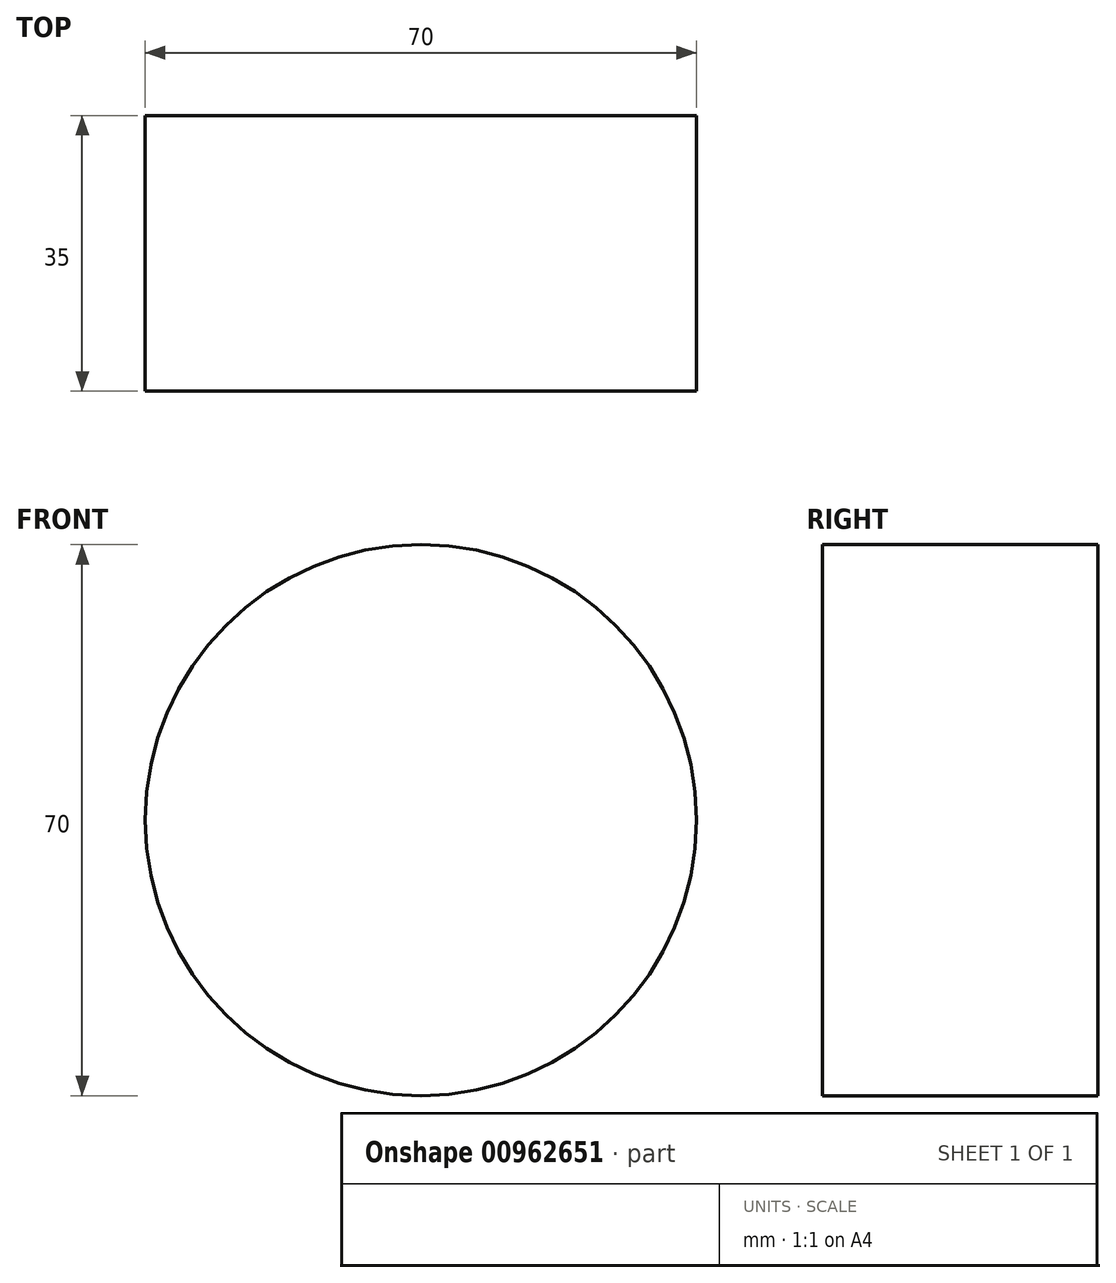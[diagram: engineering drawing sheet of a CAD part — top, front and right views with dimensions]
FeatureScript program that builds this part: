
annotation { "Feature Type Name" : "Feature", "Feature Type Description" : "" }
export const myFeature = defineFeature(function(context is Context, id is Id, definition is map)
    precondition{}
    {
        {
            var Q0;
            Q0=qCreatedBy(makeId("Front.planeOp"),FACE);
            var sketch = newSketch(context, id + "F0", { "sketchPlane" : qUnion([Q0])});
            skCircle(sketch, "E0", {"center": v(0, 0) * mm, "radius": 35 * mm});
            skSolve(sketch);
        }
        {
            var Q0;
            Q0=makeQuery(id+"F0.imprint","IMPRINT",FACE,{"disambiguationData":[TD([[makeQuery(id+"F0.imprint","IMPRINT",EDGE,{"derivedFrom":sQuery(id+"F0.wireOp",EDGE,"E0")}),1.0]])]});
            extrude(context, id + "F1", {"entities" : qUnion([Q0]), "depth" : 35 * mm, "offsetDistance" : 25.4 * mm});
        }
    });
